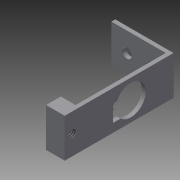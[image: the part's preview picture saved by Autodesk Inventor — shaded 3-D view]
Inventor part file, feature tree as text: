
AUTODESK INVENTOR PART (.ipt)
format: ipt  version: 2015 (Build 190159000, 159)  size: 138,240 bytes
history: native  units: in
note: dims shown in document units (in); Inventor stores cm internally (conversion verified against a paired STEP export)
features: sketch x5, extrude x4, hole x1, projected_geometry x1
ambient origin geometry x8: Origin, YZ Plane, XZ Plane, XY Plane, X Axis, Y Axis, Z Axis, Center Point
bodies: Solid1 (feature_tree)
feature tree (11):
  extrude  "Extrusion1"  Depth=0.75in
  extrude  "Extrusion2"  Depth=0.125in
  extrude  "Extrusion3"  Depth=0.25in
  extrude  "Extrusion4"  Depth=0.05in TaperAngle=0.0deg
  hole  "Hole1"  [1 undecoded]
  sketch  "Sketch1"  dims[d0=0.5in d1=0.75in]
  sketch  "Sketch2"  dims[d2=0.125in d3=0.125in]
  sketch  "Sketch3"  dims[d4=0.25in d5=0.2in]
  sketch  "Sketch4"  dims[d6=0.3in d7=0.05in d8=0.0in]
  sketch  "Sketch5"  dims[d9=0.05in d10=1.35in d11=0.0in d19=1.0in d20=0.0in d21=0.386in d22=0.5in d23=0.25in d24=0.14in d25=0.096in d26=0.08in d27=0.037in d28=0.14in d29=0.66in d30=0.19in d31=0.0in d33=0.19in d35=0.5in d38=0.25in d39=0.098in d40=0.25in d41=0.375in d42=0.25in d43=0.5635in d44=0.375in d45=0.8108in d46=0.092in]
  projected_geometry  "Projected Loop1"
note: 1 required parameter value undecoded (feature->parameter linkage not recoverable at this tier; creation-order binding heuristic only, values carry confidence <= 0.55)
